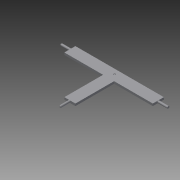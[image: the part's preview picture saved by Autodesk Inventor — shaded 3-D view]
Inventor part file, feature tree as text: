
AUTODESK INVENTOR PART (.ipt)
format: ipt  version: 2015 (Build 190159000, 159)  size: 107,008 bytes
history: native  units: in
note: dims shown in document units (in); Inventor stores cm internally (conversion verified against a paired STEP export)
features: extrude x3, sketch x3, fillet x2, pattern_circular x1
ambient origin geometry x8: Origin, YZ Plane, XZ Plane, XY Plane, X Axis, Y Axis, Z Axis, Center Point
bodies: Solid1 (feature_tree)
feature tree (9):
  extrude  "Extrusion1"  Depth=1.25in
  extrude  "Extrusion3"  Depth=0.25in
  extrude  "Extrusion4"  Depth=0.125in
  pattern_circular  "Circular Pattern2"  [2 undecoded]
  fillet  "Fillet1"  Radius=0.675in
  fillet  "Fillet2"  Radius=5.0in
  sketch  "Sketch1"  dims[d0=10.0in d1=1.25in]
  sketch  "Sketch3"  dims[d2=0.25in d3=0.0in d5=0.625in]
  sketch  "Sketch4"  dims[d6=5.0in d7=0.625in d8=5.0in d13=0.675in d14=5.0in d15=0.05in d16=0.0in d21=0.625in d22=0.125in d23=1.125in d24=0.0in d25=1.1811in d26=180.0deg d28=0.125in d29=0.125in]
note: 2 required parameter values undecoded (feature->parameter linkage not recoverable at this tier; creation-order binding heuristic only, values carry confidence <= 0.55)
